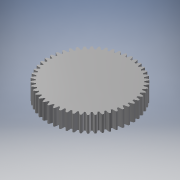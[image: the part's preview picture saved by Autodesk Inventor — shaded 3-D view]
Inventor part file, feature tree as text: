
AUTODESK INVENTOR PART (.ipt)
format: ipt  version: 2018 (Build 220112000, 112)  size: 341,504 bytes
history: native  units: mm (DEFAULTED — no unit token found)
features: plane x3, other x3, sketch x2, extrude x1
ambient origin geometry x8: Origin, YZ Plane, XZ Plane, XY Plane, X Axis, Y Axis, Z Axis, Center Point
bodies: Solid1 (feature_tree)
feature tree (9):
  extrude  "Extrusion1"  Depth=20.0mm TaperAngle=0.0deg
  plane  "Work Plane2"
  plane  "Work Plane8"
  plane  "Work Plane9"
  other  "Engranaje recto"
  sketch  "Sketch1"  dims[d0=104.0mm d1=20.0mm d2=0.0mm]
  sketch  "Sketch2"  dims[d3=100.0mm d4=10.0mm d5=0.0mm d16=70.0mm d17=0.0mm d34=0.628319mm d39=0.0mm d41=0.0mm d43=70.0mm d46=70.0mm d47=0.0mm d48=0.0mm]
  other  "Srf1"
  other  "Diámetro de separación"
